# Revit family: JNRZHSA-PV-All
name_source: partatom
category: Mechanical Equipment
units: mm (PartAtom-declared; Revit-internal decimal feet)

## family parameters
Always vertical = Yes
Cut with Voids When Loaded = No
OmniClass Number = 23.40.40.11.17
OmniClass Title = Refrigerated Cases
Part Type = Normal
Room Calculation Point = No
Round Connector Dimension = Use Radius
Shared = No
Work Plane-Based = Yes

## types (4) — shared parameters
22" Shelf = Yes
Certifications = NSF 7, UL471, CSA
Condensing  Data Volts = 208 V
Condensing Data  Phase = 1
Condensing Frequency (Hz) = 60 (Hz)
DATE = 02/10/2016
Default Elevation = 48"
Defrosts Per Day_2 = 1
Description = Narrow Reach-In Self-Contained Merchandiser
Discharge Air (°F) = -8°F
Discharge Air Velocity (FPM) = 300 (FPM)
EQUIPMENT DESCRIPTION = Narrow Reach-In Self-Contained Merchandiser
EQUIPMENT MARK = JNRZHSA-PV
Electric Defrost Fail-Safe = 45 (Min)
Electric Defrost Termination Temp (°F) = 48°F
GLASS = Glass
Height = 82 1/2"
Item Description = Narrow Reach-In Self-Contained Merchandiser
Legend Number = JNRZHSA-PV
Manufacturer = HILL PHOENIX
Model = JNRZHSA-PV
PAINTED METAL UPPER SHELF = PAINTED SHELVES
Provided Overcurrent Protection = 30
REFRIGERATION PIPING = COPPER PIPE
Refrigerant = R404A
STAINLESS STEEL = GALVANIZED STEEL
Superheat Set Point @ Bulb (F) = 3-5°F
System Data Frequency (Hz) = 60 (Hz)
System Data Phase = 1
System Data Volts = 208 V
URL = http://www.hillphoenix.com
Width = 34 7/8"

## per-type parameters (varying)
| type | 24hr Energy Usage (kWh) | CENTER LINE & DRAIN | Condenser | DOOR CONFIGURATION | Horsepower | Lbs. of Refrigerant | Length | Locked Rotor (LRA) Amps | NUMBER OF DOORS | Running Load (RLA) Amps |
| 2 Door | 20.1 | 30" | 15" | MASTER DOOR : 30" X 68 3/8" 2 DOOR A SWING (LEFT OPENING) | 3/4 | 2.8 | 60" | 17 A | 2 | 9 A |
| 3 Door | 30.0 | 45" | 30" | MASTER DOOR : 30" X 68 3/8" 3 DOOR A SWING (LEFT OPENING) | 1 | 3.4 | 90" | 17 A | 3 | 9 A |
| 4 Door | 34.1 | 60" | 45" | MASTER DOOR : 30" X 68 3/8" 4 DOOR A SWING (LEFT OPENING) | 1-1/4 | 3.7 | 120" | 29 A | 4 | 13 A |
| 5 Door | 44.0 | 75" | 60" | MASTER DOOR : 30" X 68 3/8" 5 DOOR A SWING (LEFT OPENING) | 2 | 6.2 | 150" | 34 A | 5 | 12 A |

## geometry (parser evidence)
native form markers: Blend x8, Sweep x5
no freeform markers — native parametric forms only
